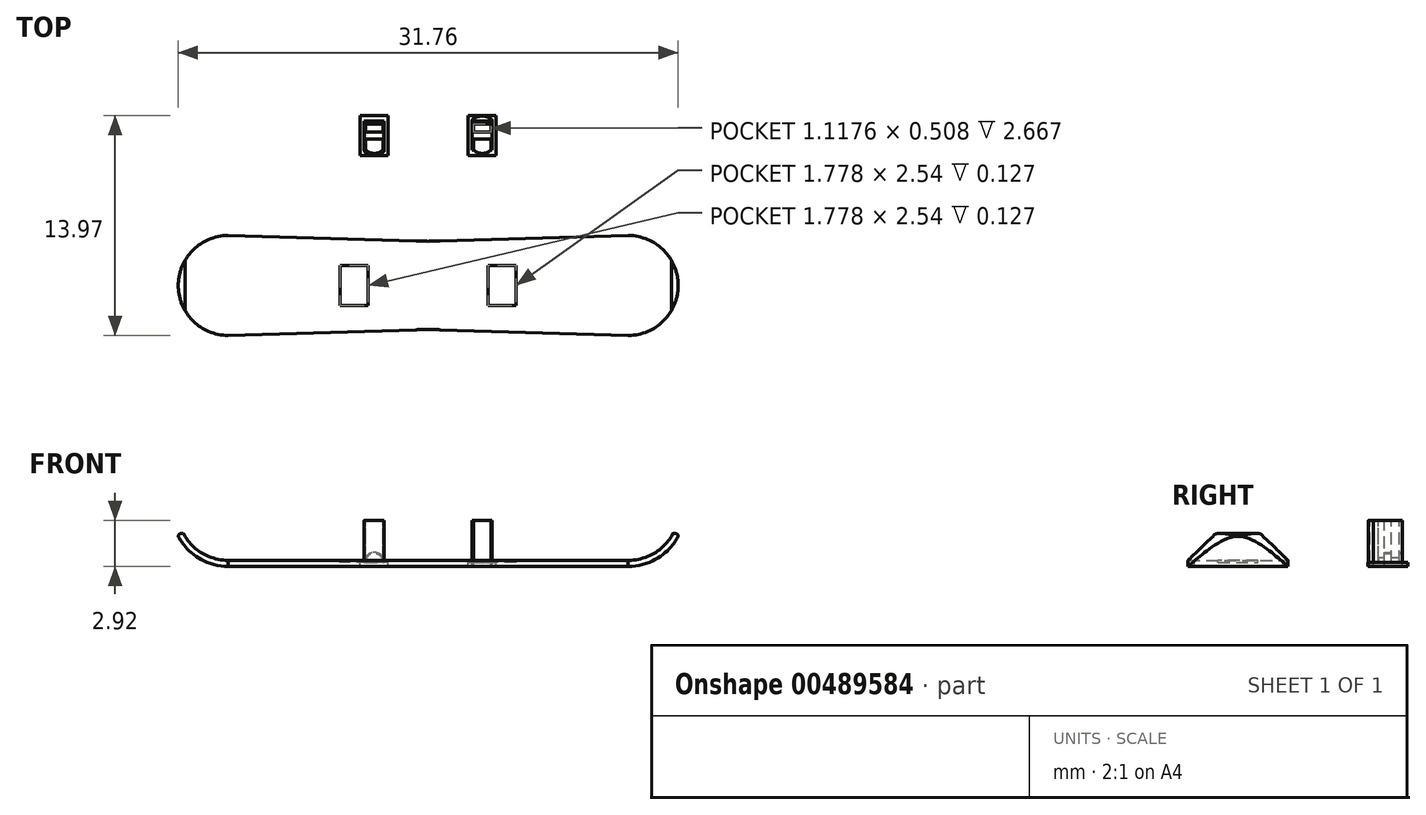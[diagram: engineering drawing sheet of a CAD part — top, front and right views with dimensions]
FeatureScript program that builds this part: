
annotation { "Feature Type Name" : "Feature", "Feature Type Description" : "" }
export const myFeature = defineFeature(function(context is Context, id is Id, definition is map)
    precondition{}
    {
        {
            var Q0;
            Q0=qCreatedBy(makeId("Top.planeOp"),FACE);
            var sketch = newSketch(context, id + "F0", { "sketchPlane" : qUnion([Q0])});
            skLineSegment(sketch, "E0", {"start": v(0, 0) * mm, "end": v(-12.7, 0) * mm, "construction": true});
            skLineSegment(sketch, "E1", {"start": v(-12.7, 0) * mm, "end": v(-12.7, -6.35) * mm});
            skLineSegment(sketch, "E2", {"start": v(-12.7, -6.35) * mm, "end": v(12.7, -6.35) * mm, "construction": true});
            skLineSegment(sketch, "E3", {"start": v(12.7, -6.35) * mm, "end": v(12.7, 0) * mm});
            skLineSegment(sketch, "E4", {"start": v(12.7, 0) * mm, "end": v(0, 0) * mm, "construction": true});
            skArc(sketch, "E5", {"start": v(-12.7, 0) * mm, "mid": v(-15.88, -3.18) * mm, "end": v(-12.7, -6.35) * mm});
            skArc(sketch, "E6", {"start": v(12.7, -6.35) * mm, "mid": v(15.87, -3.17) * mm, "end": v(12.7, 0) * mm});
            skLineSegment(sketch, "E7", {"start": v(0, 0) * mm, "end": v(0, -0.38) * mm, "construction": true});
            skLineSegment(sketch, "E8", {"start": v(0, -6.35) * mm, "end": v(0, -5.97) * mm, "construction": true});
            skPoint(sketch, "E8.endSnap0", {"position": v(0, -6.35) * mm});
            skLineSegment(sketch, "E9", {"start": v(-6.35, 0) * mm, "end": v(-6.35, -0.2) * mm, "construction": true});
            skLineSegment(sketch, "E10", {"start": v(-12.7, 0) * mm, "end": v(-6.35, -0.2) * mm});
            skLineSegment(sketch, "E11", {"start": v(-6.35, -0.2) * mm, "end": v(0, -0.38) * mm});
            skLineSegment(sketch, "E12", {"start": v(-6.35, -6.35) * mm, "end": v(-6.35, -6.16) * mm, "construction": true});
            skLineSegment(sketch, "E13", {"start": v(-12.7, -6.35) * mm, "end": v(-6.35, -6.16) * mm});
            skLineSegment(sketch, "E14", {"start": v(-6.35, -6.16) * mm, "end": v(0, -5.97) * mm});
            skLineSegment(sketch, "E15", {"start": v(6.35, 0) * mm, "end": v(6.35, -0.2) * mm, "construction": true});
            skLineSegment(sketch, "E16", {"start": v(6.35, -6.35) * mm, "end": v(6.35, -6.16) * mm, "construction": true});
            skLineSegment(sketch, "E17", {"start": v(0, -0.38) * mm, "end": v(6.35, -0.2) * mm});
            skLineSegment(sketch, "E18", {"start": v(6.35, -0.2) * mm, "end": v(12.7, 0) * mm});
            skLineSegment(sketch, "E19", {"start": v(12.7, -6.35) * mm, "end": v(6.35, -6.16) * mm});
            skLineSegment(sketch, "E20", {"start": v(0, -5.97) * mm, "end": v(6.35, -6.16) * mm});
            skLineSegment(sketch, "E21", {"start": v(0, 0) * mm, "end": v(0, 5.08) * mm, "construction": true});
            skLineSegment(sketch, "E22", {"start": v(-2.54, 5.08) * mm, "end": v(0, 5.08) * mm, "construction": true});
            skLineSegment(sketch, "E23.bottom", {"start": v(-2.54, 5.08) * mm, "end": v(-4.32, 5.08) * mm});
            skLineSegment(sketch, "E23.top", {"start": v(-2.54, 7.62) * mm, "end": v(-4.32, 7.62) * mm});
            skLineSegment(sketch, "E23.left", {"start": v(-2.54, 5.08) * mm, "end": v(-2.54, 7.62) * mm});
            skLineSegment(sketch, "E23.right", {"start": v(-4.32, 5.08) * mm, "end": v(-4.32, 7.62) * mm});
            skLineSegment(sketch, "E24", {"start": v(-4.32, 5.33) * mm, "end": v(-4.06, 5.33) * mm, "construction": true});
            skLineSegment(sketch, "E25", {"start": v(-4.06, 5.33) * mm, "end": v(-4.06, 5.08) * mm, "construction": true});
            skLineSegment(sketch, "E26", {"start": v(-2.54, 5.33) * mm, "end": v(-2.8, 5.33) * mm, "construction": true});
            skLineSegment(sketch, "E27", {"start": v(-2.8, 5.33) * mm, "end": v(-2.8, 5.08) * mm, "construction": true});
            skArc(sketch, "E28", {"start": v(-3.98, 5.27) * mm, "mid": v(-3.43, 5.11) * mm, "end": v(-2.88, 5.27) * mm});
            skLineSegment(sketch, "E29", {"start": v(-4.32, 7.37) * mm, "end": v(-4.06, 7.37) * mm, "construction": true});
            skLineSegment(sketch, "E30", {"start": v(-4.06, 7.37) * mm, "end": v(-4.06, 7.62) * mm, "construction": true});
            skLineSegment(sketch, "E31", {"start": v(-2.8, 7.62) * mm, "end": v(-2.8, 7.37) * mm, "construction": true});
            skLineSegment(sketch, "E32", {"start": v(-2.8, 7.37) * mm, "end": v(-2.54, 7.37) * mm, "construction": true});
            skArc(sketch, "E33", {"start": v(-2.88, 7.43) * mm, "mid": v(-3.43, 7.59) * mm, "end": v(-3.98, 7.43) * mm});
            skLineSegment(sketch, "E34", {"start": v(-4.06, 7.27) * mm, "end": v(-4.06, 5.43) * mm});
            skLineSegment(sketch, "E35", {"start": v(-2.8, 5.43) * mm, "end": v(-2.8, 7.27) * mm});
            skPoint(sketch, "E36.visualSharp", {"position": v(-2.8, 7.37) * mm});
            skArc(sketch, "E36.filletArc", {"start": v(-2.8, 7.27) * mm, "mid": v(-2.82, 7.36) * mm, "end": v(-2.88, 7.43) * mm});
            skPoint(sketch, "E37.visualSharp", {"position": v(-4.06, 7.37) * mm});
            skArc(sketch, "E37.filletArc", {"start": v(-3.98, 7.43) * mm, "mid": v(-4.04, 7.36) * mm, "end": v(-4.06, 7.27) * mm});
            skPoint(sketch, "E38.visualSharp", {"position": v(-4.06, 5.33) * mm});
            skArc(sketch, "E38.filletArc", {"start": v(-4.06, 5.43) * mm, "mid": v(-4.04, 5.34) * mm, "end": v(-3.98, 5.27) * mm});
            skPoint(sketch, "E39.visualSharp", {"position": v(-2.8, 5.33) * mm});
            skArc(sketch, "E39.filletArc", {"start": v(-2.88, 5.27) * mm, "mid": v(-2.82, 5.34) * mm, "end": v(-2.8, 5.43) * mm});
            skLineSegment(sketch, "E40", {"start": v(-4.06, 7.27) * mm, "end": v(-2.8, 7.27) * mm});
            skLineSegment(sketch, "E41", {"start": v(-2.8, 7.07) * mm, "end": v(-4.06, 7.07) * mm});
            skLineSegment(sketch, "E42", {"start": v(-4.06, 6.56) * mm, "end": v(-2.8, 6.56) * mm});
            skLineSegment(sketch, "E43", {"start": v(-4.06, 6.11) * mm, "end": v(-2.8, 6.11) * mm});
            skLineSegment(sketch, "E44", {"start": v(-4.06, 5.43) * mm, "end": v(-3.99, 5.43) * mm});
            skLineSegment(sketch, "E45", {"start": v(-2.87, 5.43) * mm, "end": v(-2.8, 5.43) * mm});
            skArc(sketch, "E46", {"start": v(-3.99, 5.43) * mm, "mid": v(-3.43, 5.21) * mm, "end": v(-2.87, 5.43) * mm});
            skArc(sketch, "E47.MirrorCS", {"start": v(4.06, 5.43) * mm, "mid": v(4.04, 5.34) * mm, "end": v(3.98, 5.27) * mm});
            skArc(sketch, "E48.MirrorCS", {"start": v(3.98, 7.43) * mm, "mid": v(4.04, 7.36) * mm, "end": v(4.06, 7.27) * mm});
            skArc(sketch, "E49.MirrorCS", {"start": v(2.8, 7.27) * mm, "mid": v(2.82, 7.36) * mm, "end": v(2.88, 7.43) * mm});
            skLineSegment(sketch, "E50.MirrorCS", {"start": v(4.06, 5.43) * mm, "end": v(3.99, 5.43) * mm});
            skArc(sketch, "E51.MirrorCS", {"start": v(2.88, 5.27) * mm, "mid": v(2.82, 5.34) * mm, "end": v(2.8, 5.43) * mm});
            skLineSegment(sketch, "E52.MirrorCS", {"start": v(2.87, 5.43) * mm, "end": v(2.8, 5.43) * mm});
            skLineSegment(sketch, "E53.MirrorCS", {"start": v(2.8, 5.33) * mm, "end": v(2.8, 5.08) * mm, "construction": true});
            skLineSegment(sketch, "E54.MirrorCS", {"start": v(4.06, 5.33) * mm, "end": v(4.06, 5.08) * mm, "construction": true});
            skLineSegment(sketch, "E55.MirrorCS", {"start": v(2.8, 7.62) * mm, "end": v(2.8, 7.37) * mm, "construction": true});
            skLineSegment(sketch, "E56.MirrorCS", {"start": v(4.06, 7.37) * mm, "end": v(4.06, 7.62) * mm, "construction": true});
            skLineSegment(sketch, "E57.MirrorCS", {"start": v(2.8, 7.07) * mm, "end": v(4.06, 7.07) * mm});
            skLineSegment(sketch, "E58.MirrorCS", {"start": v(4.06, 7.27) * mm, "end": v(2.8, 7.27) * mm});
            skLineSegment(sketch, "E59.MirrorCS", {"start": v(2.8, 7.37) * mm, "end": v(2.54, 7.37) * mm, "construction": true});
            skLineSegment(sketch, "E60.MirrorCS", {"start": v(4.32, 7.37) * mm, "end": v(4.06, 7.37) * mm, "construction": true});
            skLineSegment(sketch, "E61.MirrorCS", {"start": v(4.32, 5.33) * mm, "end": v(4.06, 5.33) * mm, "construction": true});
            skLineSegment(sketch, "E62.MirrorCS", {"start": v(2.54, 5.33) * mm, "end": v(2.8, 5.33) * mm, "construction": true});
            skPoint(sketch, "E63.MirrorP", {"position": v(2.8, 7.37) * mm});
            skLineSegment(sketch, "E64.MirrorCS", {"start": v(2.54, 5.08) * mm, "end": v(2.54, 7.62) * mm});
            skArc(sketch, "E65.MirrorCS", {"start": v(3.99, 5.43) * mm, "mid": v(3.43, 5.21) * mm, "end": v(2.87, 5.43) * mm});
            skLineSegment(sketch, "E66.MirrorCS", {"start": v(2.54, 7.62) * mm, "end": v(4.32, 7.62) * mm});
            skLineSegment(sketch, "E67.MirrorCS", {"start": v(4.32, 5.08) * mm, "end": v(4.32, 7.62) * mm});
            skLineSegment(sketch, "E68.MirrorCS", {"start": v(2.8, 5.43) * mm, "end": v(2.8, 7.27) * mm});
            skArc(sketch, "E69.MirrorCS", {"start": v(2.88, 7.43) * mm, "mid": v(3.43, 7.59) * mm, "end": v(3.98, 7.43) * mm});
            skLineSegment(sketch, "E70.MirrorCS", {"start": v(2.54, 5.08) * mm, "end": v(0, 5.08) * mm, "construction": true});
            skLineSegment(sketch, "E71.MirrorCS", {"start": v(4.06, 6.11) * mm, "end": v(2.8, 6.11) * mm});
            skLineSegment(sketch, "E72.MirrorCS", {"start": v(4.06, 6.56) * mm, "end": v(2.8, 6.56) * mm});
            skPoint(sketch, "E73.MirrorP", {"position": v(2.8, 5.33) * mm});
            skArc(sketch, "E74.MirrorCS", {"start": v(3.98, 5.27) * mm, "mid": v(3.43, 5.11) * mm, "end": v(2.88, 5.27) * mm});
            skPoint(sketch, "E75.MirrorP", {"position": v(4.06, 7.37) * mm});
            skLineSegment(sketch, "E76.MirrorCS", {"start": v(4.06, 7.27) * mm, "end": v(4.06, 5.43) * mm});
            skLineSegment(sketch, "E77.MirrorCS", {"start": v(2.54, 5.08) * mm, "end": v(4.32, 5.08) * mm});
            skPoint(sketch, "E78.MirrorP", {"position": v(4.06, 5.33) * mm});
            skLineSegment(sketch, "E79", {"start": v(-2.87, 5.43) * mm, "end": v(-2.87, 7.27) * mm});
            skLineSegment(sketch, "E80", {"start": v(-3.99, 5.43) * mm, "end": v(-3.99, 7.27) * mm});
            skLineSegment(sketch, "E81", {"start": v(2.87, 5.43) * mm, "end": v(2.87, 7.27) * mm});
            skLineSegment(sketch, "E82", {"start": v(3.99, 5.43) * mm, "end": v(3.99, 7.27) * mm});
            skSolve(sketch);
        }
        {
            var Q0;
            Q0=makeQuery(id+"F0.imprint","IMPRINT",FACE,{"disambiguationData":[TD([[makeQuery(id+"F0.imprint","IMPRINT",EDGE,{"derivedFrom":sQuery(id+"F0.wireOp",EDGE,"E1")}),-1.0]])]});
            var Q1;
            Q1=makeQuery(id+"F0.imprint","IMPRINT",FACE,{"disambiguationData":[TD([[makeQuery(id+"F0.imprint","IMPRINT",EDGE,{"derivedFrom":sQuery(id+"F0.wireOp",EDGE,"E3")}),-1.0]])]});
            var Q2;
            Q2=makeQuery(id+"F0.imprint","IMPRINT",FACE,{"disambiguationData":[TD([[makeQuery(id+"F0.imprint","IMPRINT",EDGE,{"derivedFrom":sQuery(id+"F0.wireOp",EDGE,"E1")}),1.0]])]});
            extrude(context, id + "F1", {"entities" : qUnion([Q0, Q1, Q2]), "oppositeDirection" : true, "depth" : 9.84 * mm});
        }
        {
            var Q0;
            Q0=qCreatedBy(makeId("Front.planeOp"),FACE);
            var sketch = newSketch(context, id + "F2", { "sketchPlane" : qUnion([Q0])});
            skLineSegment(sketch, "E83", {"start": v(0, 0) * mm, "end": v(0, -2.54) * mm, "construction": true});
            skLineSegment(sketch, "E84", {"start": v(0, -2.54) * mm, "end": v(-12.7, -2.54) * mm});
            skLineSegment(sketch, "E85", {"start": v(0, -2.54) * mm, "end": v(12.7, -2.54) * mm});
            skLineSegment(sketch, "E86", {"start": v(-12.7, -2.54) * mm, "end": v(-12.7, 0) * mm, "construction": true});
            skLineSegment(sketch, "E87", {"start": v(-12.7, 0) * mm, "end": v(-15.88, 0) * mm, "construction": true});
            skArc(sketch, "E88", {"start": v(-15.88, 0) * mm, "mid": v(-14.73, -1.83) * mm, "end": v(-12.7, -2.54) * mm});
            skLineSegment(sketch, "E89", {"start": v(12.7, -2.54) * mm, "end": v(12.7, 0) * mm, "construction": true});
            skLineSegment(sketch, "E90", {"start": v(12.7, 0) * mm, "end": v(15.88, 0) * mm, "construction": true});
            skArc(sketch, "E91", {"start": v(12.7, -2.54) * mm, "mid": v(14.73, -1.83) * mm, "end": v(15.88, 0) * mm});
            skLineSegment(sketch, "E92", {"start": v(0, -2.54) * mm, "end": v(0, -2.92) * mm, "construction": true});
            skLineSegment(sketch, "E93", {"start": v(0, -2.92) * mm, "end": v(-12.7, -2.92) * mm});
            skLineSegment(sketch, "E94", {"start": v(0, -2.92) * mm, "end": v(12.7, -2.92) * mm});
            skLineSegment(sketch, "E95", {"start": v(-12.7, -1.02) * mm, "end": v(-15.87, -1.02) * mm, "construction": true});
            skArc(sketch, "E96", {"start": v(-15.87, -1.02) * mm, "mid": v(-14.55, -2.4) * mm, "end": v(-12.7, -2.92) * mm});
            skArc(sketch, "E97", {"start": v(-15.46, -1.02) * mm, "mid": v(-15.67, -0.81) * mm, "end": v(-15.87, -1.02) * mm});
            skLineSegment(sketch, "E98", {"start": v(12.7, -1.02) * mm, "end": v(15.87, -1.02) * mm, "construction": true});
            skArc(sketch, "E99", {"start": v(12.7, -2.92) * mm, "mid": v(14.55, -2.4) * mm, "end": v(15.87, -1.02) * mm});
            skArc(sketch, "E100", {"start": v(15.88, -1.02) * mm, "mid": v(15.67, -0.81) * mm, "end": v(15.46, -1.02) * mm});
            skLineSegment(sketch, "E101", {"start": v(15.88, -1.02) * mm, "end": v(15.88, 0) * mm});
            skLineSegment(sketch, "E102", {"start": v(15.88, 0) * mm, "end": v(-15.88, 0) * mm});
            skLineSegment(sketch, "E103", {"start": v(-15.88, 0) * mm, "end": v(-15.88, -1.02) * mm});
            skLineSegment(sketch, "E104", {"start": v(-15.87, -1.02) * mm, "end": v(-15.87, -9.84) * mm});
            skLineSegment(sketch, "E105", {"start": v(-15.87, -9.84) * mm, "end": v(15.88, -9.84) * mm});
            skLineSegment(sketch, "E106", {"start": v(15.88, -9.84) * mm, "end": v(15.87, -1.02) * mm});
            skSolve(sketch);
        }
        {
            var Q0;
            {var subQ1=sQuery(id+"F2.wireOp",EDGE,"E84");Q0=makeQuery(id+"F2.imprint","IMPRINT",FACE,{"disambiguationData":[TD([[makeQuery(id+"F2.imprint","IMPRINT",EDGE,{"derivedFrom":subQ1}),-1.0]])]});}
            var Q1;
            {var subQ0=sQuery(id+"F2.wireOp",EDGE,"E103");Q1=makeQuery(id+"F2.imprint","IMPRINT",FACE,{"disambiguationData":[TD([[makeQuery(id+"F2.imprint","IMPRINT",EDGE,{"derivedFrom":subQ0}),1.0]])]});}
            var Q2;
            Q2=makeQuery(id+"F2.imprint","IMPRINT",FACE,{"disambiguationData":[TD([[makeQuery(id+"F2.imprint","IMPRINT",EDGE,{"derivedFrom":sQuery(id+"F2.wireOp",EDGE,"E93")}),1.0]])]});
            var Q3;
            {var subQ0=sQuery(id+"F2.wireOp",EDGE,"E101");Q3=makeQuery(id+"F2.imprint","IMPRINT",FACE,{"disambiguationData":[TD([[makeQuery(id+"F2.imprint","IMPRINT",EDGE,{"derivedFrom":subQ0}),1.0]])]});}
            extrude(context, id + "F3", {"entities" : qUnion([Q0, Q1, Q2, Q3]), "operationType" : NewBodyOperationType.REMOVE, "depth" : 25.4 * mm});
        }
        {
            var Q0;
            Q0=qCreatedBy(makeId("Top.planeOp"),FACE);
            var sketch = newSketch(context, id + "F4", { "sketchPlane" : qUnion([Q0])});
            skLineSegment(sketch, "E107", {"start": v(0, 0) * mm, "end": v(0, -3.18) * mm, "construction": true});
            skLineSegment(sketch, "E108", {"start": v(0, -3.18) * mm, "end": v(-3.8, -3.18) * mm, "construction": true});
            skLineSegment(sketch, "E109", {"start": v(0, -3.18) * mm, "end": v(3.8, -3.18) * mm, "construction": true});
            skLineSegment(sketch, "E110", {"start": v(-3.8, -3.18) * mm, "end": v(-3.8, -1.9) * mm});
            skLineSegment(sketch, "E111", {"start": v(-3.8, -1.9) * mm, "end": v(-5.59, -1.9) * mm});
            skLineSegment(sketch, "E112", {"start": v(-5.59, -1.9) * mm, "end": v(-5.59, -4.45) * mm});
            skLineSegment(sketch, "E113", {"start": v(-5.59, -4.45) * mm, "end": v(-3.8, -4.45) * mm});
            skLineSegment(sketch, "E114", {"start": v(-3.8, -4.45) * mm, "end": v(-3.8, -3.18) * mm});
            skLineSegment(sketch, "E115", {"start": v(3.8, -3.18) * mm, "end": v(3.8, -1.9) * mm});
            skLineSegment(sketch, "E116", {"start": v(3.8, -1.9) * mm, "end": v(5.59, -1.9) * mm});
            skLineSegment(sketch, "E117", {"start": v(5.59, -1.9) * mm, "end": v(5.59, -4.44) * mm});
            skLineSegment(sketch, "E118", {"start": v(5.59, -4.44) * mm, "end": v(3.8, -4.44) * mm});
            skLineSegment(sketch, "E119", {"start": v(3.8, -4.44) * mm, "end": v(3.8, -3.18) * mm});
            skSolve(sketch);
        }
        {
            var Q0;
            Q0 = qSketchRegion(id + "F4", true);
            extrude(context, id + "F5", {"entities" : qUnion([Q0]), "operationType" : NewBodyOperationType.REMOVE, "oppositeDirection" : true, "depth" : 2.67 * mm});
        }
        {
            var Q0;
            Q0=makeQuery(id+"F1.opExtrude","SWEPT_EDGE",EDGE,{"disambiguationData":[OSD([sQuery(id+"F0.wireOp",EDGE,"E14"),sQuery(id+"F0.wireOp",EDGE,"E20")])]});
            var Q1;
            Q1=makeQuery(id+"F1.opExtrude","SWEPT_EDGE",EDGE,{"disambiguationData":[OSD([sQuery(id+"F0.wireOp",EDGE,"E11"),sQuery(id+"F0.wireOp",EDGE,"E17")])]});
            fillet(context, id + "F6", {"entities" : qUnion([Q0, Q1]), "radius" : 25.4 * mm, "tangentPropagation" : true, "allowEdgeOverflow" : false});
        }
        {
            var Q0;
            {var subQ0=sQuery(id+"F0.wireOp",EDGE,"E57.MirrorCS");Q0=makeQuery(id+"F0.imprint","IMPRINT",FACE,{"disambiguationData":[TD([[makeQuery(id+"F0.imprint","IMPRINT",EDGE,{"derivedFrom":subQ0}),1.0]])]});}
            var Q1;
            Q1=makeQuery(id+"F0.imprint","IMPRINT",FACE,{"disambiguationData":[TD([[makeQuery(id+"F0.imprint","IMPRINT",EDGE,{"derivedFrom":sQuery(id+"F0.wireOp",EDGE,"E48.MirrorCS")}),-1.0]])]});
            var Q2;
            Q2=makeQuery(id+"F0.imprint","IMPRINT",FACE,{"disambiguationData":[TD([[makeQuery(id+"F0.imprint","IMPRINT",EDGE,{"derivedFrom":sQuery(id+"F0.wireOp",EDGE,"E33")}),1.0]])]});
            var Q3;
            Q3=makeQuery(id+"F0.imprint","IMPRINT",FACE,{"disambiguationData":[TD([[makeQuery(id+"F0.imprint","IMPRINT",EDGE,{"derivedFrom":sQuery(id+"F0.wireOp",EDGE,"E28")}),1.0]])]});
            var Q4;
            {var subQ0=sQuery(id+"F0.wireOp",EDGE,"E42");Q4=makeQuery(id+"F0.imprint","IMPRINT",FACE,{"disambiguationData":[TD([[makeQuery(id+"F0.imprint","IMPRINT",EDGE,{"derivedFrom":subQ0}),-1.0]])]});}
            var Q5;
            {var subQ0=sQuery(id+"F0.wireOp",EDGE,"E41");Q5=makeQuery(id+"F0.imprint","IMPRINT",FACE,{"disambiguationData":[TD([[makeQuery(id+"F0.imprint","IMPRINT",EDGE,{"derivedFrom":subQ0}),1.0]])]});}
            var Q6;
            {var subQ4=sQuery(id+"F0.wireOp",EDGE,"E50.MirrorCS");Q6=makeQuery(id+"F0.imprint","IMPRINT",FACE,{"disambiguationData":[TD([[makeQuery(id+"F0.imprint","IMPRINT",EDGE,{"derivedFrom":subQ4}),-1.0]])]});}
            var Q7;
            Q7=makeQuery(id+"F0.imprint","IMPRINT",FACE,{"disambiguationData":[TD([[makeQuery(id+"F0.imprint","IMPRINT",EDGE,{"derivedFrom":sQuery(id+"F0.wireOp",EDGE,"E23.bottom")}),-1.0]])]});
            var Q8;
            {var subQ5=sQuery(id+"F0.wireOp",EDGE,"E47.MirrorCS");Q8=makeQuery(id+"F0.imprint","IMPRINT",FACE,{"disambiguationData":[TD([[makeQuery(id+"F0.imprint","IMPRINT",EDGE,{"derivedFrom":subQ5}),1.0]])]});}
            var Q9;
            {var subQ0=sQuery(id+"F0.wireOp",EDGE,"E57.MirrorCS");Q9=makeQuery(id+"F0.imprint","IMPRINT",FACE,{"disambiguationData":[TD([[makeQuery(id+"F0.imprint","IMPRINT",EDGE,{"derivedFrom":subQ0}),-1.0]])]});}
            var Q10;
            {var subQ1=sQuery(id+"F0.wireOp",EDGE,"E43");Q10=makeQuery(id+"F0.imprint","IMPRINT",FACE,{"disambiguationData":[TD([[makeQuery(id+"F0.imprint","IMPRINT",EDGE,{"derivedFrom":subQ1}),-1.0]])]});}
            var Q11;
            {var subQ0=sQuery(id+"F0.wireOp",EDGE,"E40");Q11=makeQuery(id+"F0.imprint","IMPRINT",FACE,{"disambiguationData":[TD([[makeQuery(id+"F0.imprint","IMPRINT",EDGE,{"derivedFrom":subQ0}),-1.0]])]});}
            var Q12;
            Q12=makeQuery(id+"F0.imprint","IMPRINT",FACE,{"disambiguationData":[TD([[makeQuery(id+"F0.imprint","IMPRINT",EDGE,{"derivedFrom":sQuery(id+"F0.wireOp",EDGE,"E47.MirrorCS")}),-1.0]])]});
            var Q13;
            {var subQ0=sQuery(id+"F0.wireOp",EDGE,"E71.MirrorCS");Q13=makeQuery(id+"F0.imprint","IMPRINT",FACE,{"disambiguationData":[TD([[makeQuery(id+"F0.imprint","IMPRINT",EDGE,{"derivedFrom":subQ0}),-1.0]])]});}
            var Q14;
            {var subQ0=sQuery(id+"F0.wireOp",EDGE,"E65.MirrorCS");Q14=makeQuery(id+"F0.imprint","IMPRINT",FACE,{"disambiguationData":[TD([[makeQuery(id+"F0.imprint","IMPRINT",EDGE,{"derivedFrom":subQ0}),-1.0]])]});}
            var Q15;
            {var subQ0=sQuery(id+"F0.wireOp",EDGE,"E52.MirrorCS");Q15=makeQuery(id+"F0.imprint","IMPRINT",FACE,{"disambiguationData":[TD([[makeQuery(id+"F0.imprint","IMPRINT",EDGE,{"derivedFrom":subQ0}),-1.0]])]});}
            extrude(context, id + "F7", {"entities" : qUnion([Q0, Q1, Q2, Q3, Q4, Q5, Q6, Q7, Q8, Q9, Q10, Q11, Q12, Q13, Q14, Q15]), "oppositeDirection" : true, "depth" : 2.92 * mm});
        }
        {
            var Q0;
            {var subQ5=sQuery(id+"F0.wireOp",EDGE,"E46");Q0=makeQuery(id+"F0.imprint","IMPRINT",FACE,{"disambiguationData":[TD([[makeQuery(id+"F0.imprint","IMPRINT",EDGE,{"derivedFrom":subQ5}),1.0]])]});}
            var Q1;
            Q1=makeQuery(id+"F0.imprint","IMPRINT",FACE,{"disambiguationData":[TD([[makeQuery(id+"F0.imprint","IMPRINT",EDGE,{"derivedFrom":sQuery(id+"F0.wireOp",EDGE,"E23.bottom")}),-1.0]])]});
            var Q2;
            {var subQ0=sQuery(id+"F0.wireOp",EDGE,"E79");var subQ1=sQuery(id+"F0.wireOp",EDGE,"E41");var subQ2=makeQuery(id+"F0.imprint","INTERSECT",VERTEX,{"derivedFrom":[subQ1,subQ0]});Q2=makeQuery(id+"F0.imprint","IMPRINT",FACE,{"disambiguationData":[TD([[makeQuery(id+"F0.imprint","IMPRINT",EDGE,{"disambiguationData":[TD([[subQ2,-1.0]])],"derivedFrom":subQ1}),1.0]])]});}
            var Q3;
            Q3=makeQuery(id+"F0.imprint","IMPRINT",FACE,{"disambiguationData":[TD([[makeQuery(id+"F0.imprint","IMPRINT",EDGE,{"derivedFrom":sQuery(id+"F0.wireOp",EDGE,"E33")}),1.0]])]});
            extrude(context, id + "F8", {"entities" : qUnion([Q0, Q1, Q2, Q3]), "operationType" : NewBodyOperationType.REMOVE, "oppositeDirection" : true, "depth" : 2.67 * mm});
        }
        {
            var Q0;
            {var subQ0=sQuery(id+"F0.wireOp",EDGE,"E81");var subQ1=sQuery(id+"F0.wireOp",EDGE,"E57.MirrorCS");var subQ2=makeQuery(id+"F0.imprint","INTERSECT",VERTEX,{"derivedFrom":[subQ1,subQ0]});Q0=makeQuery(id+"F0.imprint","IMPRINT",FACE,{"disambiguationData":[TD([[makeQuery(id+"F0.imprint","IMPRINT",EDGE,{"disambiguationData":[TD([[subQ2,-1.0]])],"derivedFrom":subQ1}),-1.0]])]});}
            var Q1;
            {var subQ8=sQuery(id+"F0.wireOp",EDGE,"E47.MirrorCS");Q1=makeQuery(id+"F0.imprint","IMPRINT",FACE,{"disambiguationData":[TD([[makeQuery(id+"F0.imprint","IMPRINT",EDGE,{"derivedFrom":subQ8}),1.0]])]});}
            var Q2;
            {var subQ3=sQuery(id+"F0.wireOp",EDGE,"E48.MirrorCS");Q2=makeQuery(id+"F0.imprint","IMPRINT",FACE,{"disambiguationData":[TD([[makeQuery(id+"F0.imprint","IMPRINT",EDGE,{"derivedFrom":subQ3}),-1.0]])]});}
            var Q3;
            {var subQ0=sQuery(id+"F0.wireOp",EDGE,"E65.MirrorCS");Q3=makeQuery(id+"F0.imprint","IMPRINT",FACE,{"disambiguationData":[TD([[makeQuery(id+"F0.imprint","IMPRINT",EDGE,{"derivedFrom":subQ0}),-1.0]])]});}
            extrude(context, id + "F9", {"entities" : qUnion([Q0, Q1, Q2, Q3]), "operationType" : NewBodyOperationType.REMOVE, "oppositeDirection" : true, "depth" : 2.67 * mm});
        }
        {
            var Q0;
            Q0=makeQuery(id+"F8.boolean.opBoolean","COPY",FACE,{"derivedFrom":makeQuery(id+"F8.opExtrude","SWEPT_FACE",FACE,{"disambiguationData":[OSD([sQuery(id+"F0.wireOp",EDGE,"E40")])]})});
            var sketch = newSketch(context, id + "F10", { "sketchPlane" : qUnion([Q0])});
            skLineSegment(sketch, "E120", {"start": v(3.99, -2.67) * mm, "end": v(2.87, -2.67) * mm});
            skArc(sketch, "E121", {"start": v(3.99, -2.67) * mm, "mid": v(3.43, -2.1) * mm, "end": v(2.87, -2.67) * mm});
            skLineSegment(sketch, "E122", {"start": v(2.87, -2.67) * mm, "end": v(2.8, -2.67) * mm});
            skLineSegment(sketch, "E123", {"start": v(2.8, -2.67) * mm, "end": v(2.8, 0) * mm});
            skLineSegment(sketch, "E124", {"start": v(2.8, 0) * mm, "end": v(4.06, 0) * mm});
            skLineSegment(sketch, "E125", {"start": v(4.06, 0) * mm, "end": v(4.06, -2.67) * mm});
            skLineSegment(sketch, "E126", {"start": v(4.06, -2.67) * mm, "end": v(3.99, -2.67) * mm});
            skArc(sketch, "E127", {"start": v(4.06, -2.67) * mm, "mid": v(3.43, -2.03) * mm, "end": v(2.8, -2.67) * mm});
            skSolve(sketch);
        }
        {
            var Q0;
            Q0=makeQuery(id+"F9.boolean.opBoolean","COPY",FACE,{"derivedFrom":makeQuery(id+"F9.opExtrude","SWEPT_FACE",FACE,{"disambiguationData":[OSD([sQuery(id+"F0.wireOp",EDGE,"E58.MirrorCS")])]})});
            var sketch = newSketch(context, id + "F11", { "sketchPlane" : qUnion([Q0])});
            skLineSegment(sketch, "E128", {"start": v(-4.06, -2.67) * mm, "end": v(-3.99, -2.67) * mm});
            skLineSegment(sketch, "E129", {"start": v(-3.99, -2.67) * mm, "end": v(-2.87, -2.67) * mm});
            skLineSegment(sketch, "E130", {"start": v(-2.87, -2.67) * mm, "end": v(-2.8, -2.67) * mm});
            skArc(sketch, "E131", {"start": v(-2.87, -2.67) * mm, "mid": v(-3.43, -2.1) * mm, "end": v(-3.99, -2.67) * mm});
            skLineSegment(sketch, "E132", {"start": v(-4.06, -2.67) * mm, "end": v(-4.06, 0) * mm});
            skLineSegment(sketch, "E133", {"start": v(-4.06, 0) * mm, "end": v(-2.8, 0) * mm});
            skLineSegment(sketch, "E134", {"start": v(-2.8, 0) * mm, "end": v(-2.8, -2.67) * mm});
            skArc(sketch, "E135", {"start": v(-2.8, -2.67) * mm, "mid": v(-3.43, -2.03) * mm, "end": v(-4.06, -2.67) * mm});
            skSolve(sketch);
        }
        {
            var Q0;
            Q0=makeQuery(id+"F11.imprint","IMPRINT",FACE,{"disambiguationData":[TD([[makeQuery(id+"F11.imprint","IMPRINT",EDGE,{"derivedFrom":sQuery(id+"F11.wireOp",EDGE,"E129")}),1.0]])]});
            var Q1;
            Q1=makeQuery(id+"F11.imprint","IMPRINT",FACE,{"disambiguationData":[TD([[makeQuery(id+"F11.imprint","IMPRINT",EDGE,{"derivedFrom":sQuery(id+"F11.wireOp",EDGE,"E132")}),-1.0]])]});
            var Q2;
            Q2=makeQuery(id+"F10.imprint","IMPRINT",FACE,{"disambiguationData":[TD([[makeQuery(id+"F10.imprint","IMPRINT",EDGE,{"derivedFrom":sQuery(id+"F10.wireOp",EDGE,"E120")}),-1.0]])]});
            var Q3;
            Q3=makeQuery(id+"F10.imprint","IMPRINT",FACE,{"disambiguationData":[TD([[makeQuery(id+"F10.imprint","IMPRINT",EDGE,{"derivedFrom":sQuery(id+"F10.wireOp",EDGE,"E123")}),-1.0]])]});
            extrude(context, id + "F12", {"entities" : qUnion([Q0, Q1, Q2, Q3]), "operationType" : NewBodyOperationType.REMOVE, "oppositeDirection" : true, "depth" : 1.52 * mm});
        }
    });
